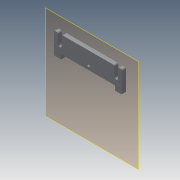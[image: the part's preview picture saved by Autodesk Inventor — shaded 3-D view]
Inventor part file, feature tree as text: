
AUTODESK INVENTOR PART (.ipt)
format: ipt  version: 2014 SP1 (Build 180222100, 222)  size: 117,760 bytes
history: native  units: in
note: dims shown in document units (in); Inventor stores cm internally (conversion verified against a paired STEP export)
features: plane x1, extrude x1, chamfer x1, sketch x1
ambient origin geometry x8: Origin, YZ Plane, XZ Plane, XY Plane, X Axis, Y Axis, Z Axis, Center Point
bodies: Solid1 (feature_tree)
feature tree (4):
  plane  "Work Plane1"
  extrude  "Extrusion1"  Depth=6.0in
  chamfer  "Chamfer1"  Distance=0.2756in
  sketch  "Sketch1"  dims[d1=3.0in d4=0.325in d7=0.3409in d8=0.0in d10=6.0in d11=0.2756in d12=0.3543in d13=0.0787in d14=0.2165in d15=0.0787in d16=0.2165in d17=2.275in d18=0.0625in d19=0.0787in d20=45.0deg]
